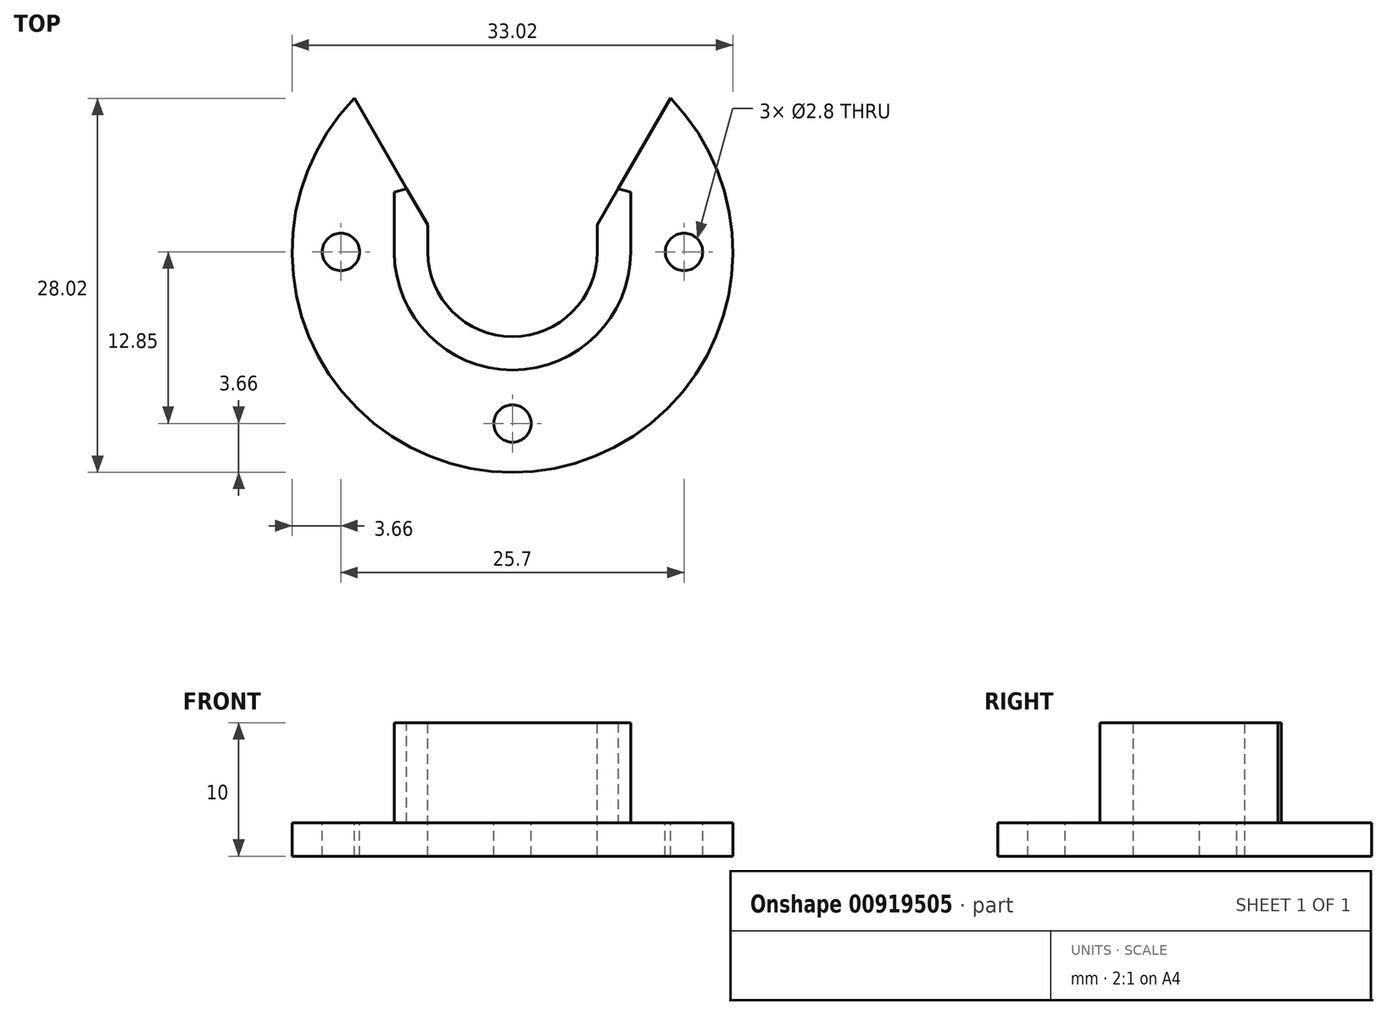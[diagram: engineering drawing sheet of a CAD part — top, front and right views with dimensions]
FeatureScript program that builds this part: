
annotation { "Feature Type Name" : "Feature", "Feature Type Description" : "" }
export const myFeature = defineFeature(function(context is Context, id is Id, definition is map)
    precondition{}
    {
        {
            var Q0;
            Q0=qCreatedBy(makeId("Top.planeOp"),FACE);
            var sketch = newSketch(context, id + "F0", { "sketchPlane" : qUnion([Q0])});
            skCircle(sketch, "E0", {"center": v(0, 0) * mm, "radius": 6.35 * mm});
            skArc(sketch, "E1", {"start": v(-8.85, 0) * mm, "mid": v(0, -8.85) * mm, "end": v(8.85, 0) * mm});
            skLineSegment(sketch, "E2", {"start": v(-8.85, 0) * mm, "end": v(-8.85, 6.35) * mm});
            skLineSegment(sketch, "E3", {"start": v(8.85, 6.35) * mm, "end": v(8.85, 0) * mm});
            skLineSegment(sketch, "E4", {"start": v(-8.85, 6.35) * mm, "end": v(-11.83, 11.51) * mm});
            skLineSegment(sketch, "E5", {"start": v(8.85, 6.35) * mm, "end": v(11.83, 11.51) * mm});
            skArc(sketch, "E6", {"start": v(-11.83, 11.51) * mm, "mid": v(0, -16.51) * mm, "end": v(11.83, 11.51) * mm});
            skLineSegment(sketch, "E7", {"start": v(-8.85, 6.35) * mm, "end": v(-6.35, 6.35) * mm});
            skLineSegment(sketch, "E8", {"start": v(-6.35, 6.35) * mm, "end": v(-6.35, 0) * mm});
            skLineSegment(sketch, "E9", {"start": v(8.85, 6.35) * mm, "end": v(6.35, 6.35) * mm});
            skLineSegment(sketch, "E10", {"start": v(6.35, 6.35) * mm, "end": v(6.35, 0) * mm});
            skLineSegment(sketch, "E11", {"start": v(-8.85, 6.35) * mm, "end": v(-6.35, 2.02) * mm});
            skLineSegment(sketch, "E12", {"start": v(8.85, 6.35) * mm, "end": v(6.35, 2.02) * mm});
            skSolve(sketch);
        }
        {
            var Q0;
            Q0=makeQuery(id+"F0.imprint","IMPRINT",FACE,{"disambiguationData":[TD([[makeQuery(id+"F0.imprint","IMPRINT",EDGE,{"derivedFrom":sQuery(id+"F0.wireOp",EDGE,"E1")}),-1.0]])]});
            var Q1;
            Q1=makeQuery(id+"F0.imprint","IMPRINT",FACE,{"disambiguationData":[TD([[makeQuery(id+"F0.imprint","IMPRINT",EDGE,{"derivedFrom":sQuery(id+"F0.wireOp",EDGE,"E1")}),1.0]])]});
            extrude(context, id + "F1", {"entities" : qUnion([Q0, Q1]), "oppositeDirection" : true, "depth" : 2.5 * mm, "offsetDistance" : 25 * mm});
        }
        {
            var Q0;
            Q0=makeQuery(id+"F0.imprint","IMPRINT",FACE,{"disambiguationData":[TD([[makeQuery(id+"F0.imprint","IMPRINT",EDGE,{"derivedFrom":sQuery(id+"F0.wireOp",EDGE,"E1")}),1.0]])]});
            extrude(context, id + "F2", {"entities" : qUnion([Q0]), "operationType" : NewBodyOperationType.ADD, "depth" : 7.5 * mm, "offsetDistance" : 25 * mm});
        }
        {
            var Q0;
            Q0=makeQuery(id+"F2.opExtrude","SWEPT_EDGE",EDGE,{"disambiguationData":[OSD([sQuery(id+"F0.wireOp",EDGE,"E2"),sQuery(id+"F0.wireOp",EDGE,"E4"),sQuery(id+"F0.wireOp",EDGE,"E7"),sQuery(id+"F0.wireOp",EDGE,"E11")])]});
            var Q1;
            Q1=makeQuery(id+"F2.opExtrude","SWEPT_EDGE",EDGE,{"disambiguationData":[OSD([sQuery(id+"F0.wireOp",EDGE,"E3"),sQuery(id+"F0.wireOp",EDGE,"E5"),sQuery(id+"F0.wireOp",EDGE,"E9"),sQuery(id+"F0.wireOp",EDGE,"E12")])]});
            chamfer(context, id + "F3", {"entities" : qUnion([Q0, Q1]), "width" : 0.5 * mm, "tangentPropagation" : true});
        }
        {
            var Q0;
            Q0=makeQuery(id+"F1.opExtrude","CAP_FACE",FACE,{"disambiguationData":[OSD([sQuery(id+"F0.wireOp",EDGE,"E0"),sQuery(id+"F0.wireOp",EDGE,"E4"),sQuery(id+"F0.wireOp",EDGE,"E5"),sQuery(id+"F0.wireOp",EDGE,"E6"),sQuery(id+"F0.wireOp",EDGE,"E8"),sQuery(id+"F0.wireOp",EDGE,"E10"),sQuery(id+"F0.wireOp",EDGE,"E11"),sQuery(id+"F0.wireOp",EDGE,"E12")])],"isStart":true});
            var sketch = newSketch(context, id + "F4", { "sketchPlane" : qUnion([Q0])});
            skPoint(sketch, "E13", {"position": v(-12.85, 0) * mm});
            skPoint(sketch, "E14", {"position": v(12.85, 0) * mm});
            skPoint(sketch, "E15", {"position": v(0, -12.85) * mm});
            skPoint(sketch, "E15.positionSnap0", {"position": v(0, -8.85) * mm});
            skCircle(sketch, "E16", {"center": v(12.85, 0) * mm, "radius": 1.4 * mm});
            skCircle(sketch, "E17", {"center": v(0, -12.85) * mm, "radius": 1.4 * mm});
            skCircle(sketch, "E18", {"center": v(-12.85, 0) * mm, "radius": 1.4 * mm});
            skSolve(sketch);
        }
        {
            var Q0;
            Q0=makeQuery(id+"F4.imprint","IMPRINT",FACE,{"disambiguationData":[TD([[makeQuery(id+"F4.imprint","IMPRINT",EDGE,{"derivedFrom":sQuery(id+"F4.wireOp",EDGE,"E18")}),1.0]])]});
            var Q1;
            Q1=makeQuery(id+"F4.imprint","IMPRINT",FACE,{"disambiguationData":[TD([[makeQuery(id+"F4.imprint","IMPRINT",EDGE,{"derivedFrom":sQuery(id+"F4.wireOp",EDGE,"E16")}),1.0]])]});
            var Q2;
            Q2=makeQuery(id+"F4.imprint","IMPRINT",FACE,{"disambiguationData":[TD([[makeQuery(id+"F4.imprint","IMPRINT",EDGE,{"derivedFrom":sQuery(id+"F4.wireOp",EDGE,"E17")}),1.0]])]});
            extrude(context, id + "F5", {"entities" : qUnion([Q0, Q1, Q2]), "operationType" : NewBodyOperationType.REMOVE, "oppositeDirection" : true, "depth" : 25 * mm, "offsetDistance" : 25 * mm});
        }
    });
